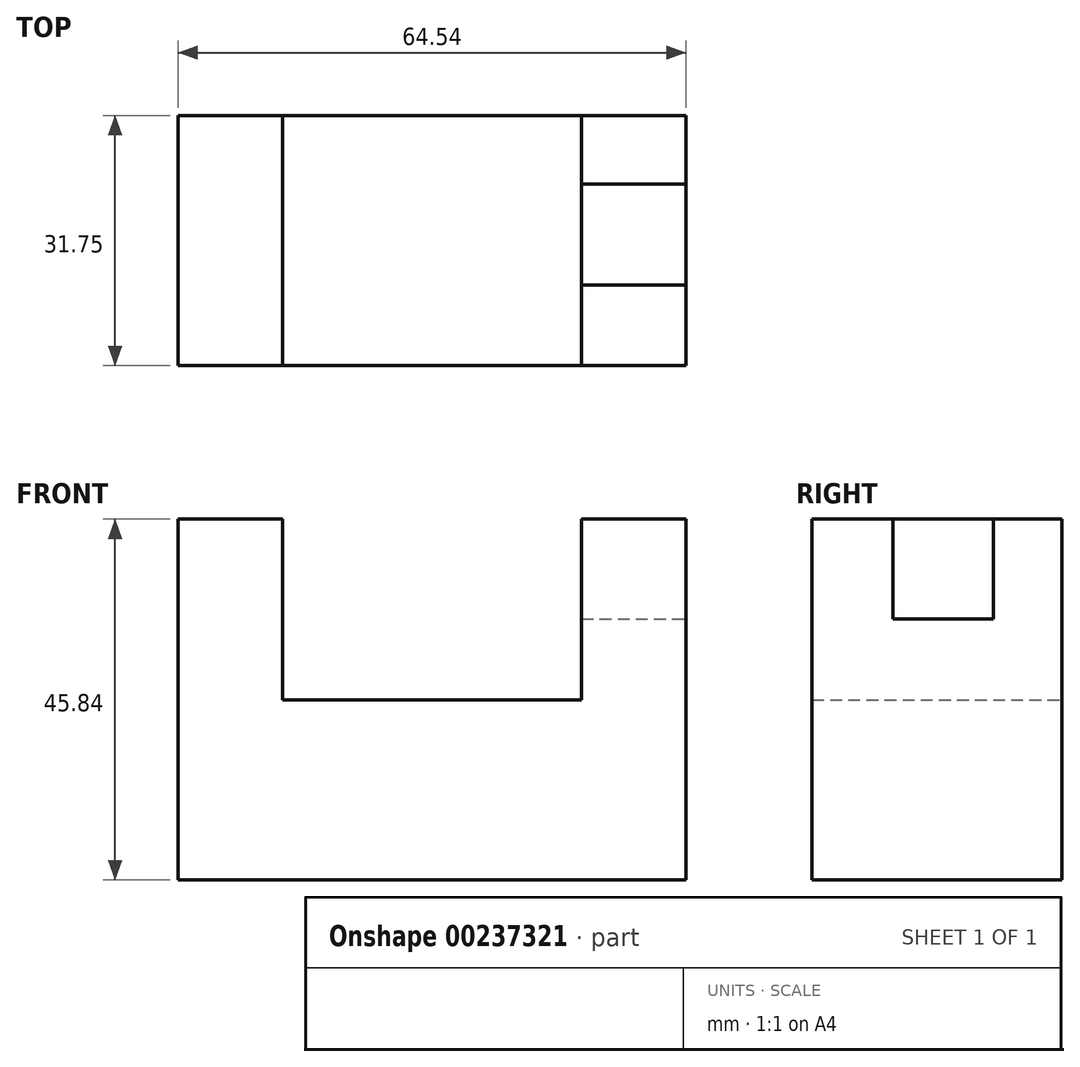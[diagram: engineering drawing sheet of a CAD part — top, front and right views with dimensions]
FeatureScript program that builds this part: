
annotation { "Feature Type Name" : "Feature", "Feature Type Description" : "" }
export const myFeature = defineFeature(function(context is Context, id is Id, definition is map)
    precondition{}
    {
        {
            var Q0;
            Q0=qCreatedBy(makeId("Front.planeOp"),FACE);
            var sketch = newSketch(context, id + "F0", { "sketchPlane" : qUnion([Q0])});
            skLineSegment(sketch, "E0.bottom", {"start": v(0, 0) * mm, "end": v(64.54, 0) * mm});
            skLineSegment(sketch, "E0.top", {"start": v(0, 45.84) * mm, "end": v(13.29, 45.84) * mm});
            skLineSegment(sketch, "E0.left", {"start": v(0, 0) * mm, "end": v(0, 45.84) * mm});
            skLineSegment(sketch, "E0.right", {"start": v(64.54, 0) * mm, "end": v(64.54, 45.84) * mm});
            skLineSegment(sketch, "E1.bottom", {"start": v(13.29, 22.87) * mm, "end": v(51.25, 22.87) * mm});
            skLineSegment(sketch, "E1.left", {"start": v(13.29, 22.87) * mm, "end": v(13.29, 45.84) * mm});
            skLineSegment(sketch, "E1.right", {"start": v(51.25, 22.87) * mm, "end": v(51.25, 45.84) * mm});
            skPoint(sketch, "E1.middle", {"position": v(32.27, 45.84) * mm});
            skPoint(sketch, "E1.top.start.orphan", {"position": v(13.29, 68.81) * mm});
            skPoint(sketch, "E2.orphan", {"position": v(51.25, 68.81) * mm});
            skLineSegment(sketch, "E3.trimOffspring", {"start": v(51.25, 45.84) * mm, "end": v(64.54, 45.84) * mm});
            skSolve(sketch);
        }
        {
            var Q0;
            Q0=makeQuery(id+"F0.imprint","IMPRINT",FACE,{"disambiguationData":[TD([[makeQuery(id+"F0.imprint","IMPRINT",EDGE,{"derivedFrom":sQuery(id+"F0.wireOp",EDGE,"E0.bottom")}),1.0]])]});
            extrude(context, id + "F1", {"entities" : qUnion([Q0]), "depth" : 31.75 * mm});
        }
        {
            var Q0;
            Q0=makeQuery(id+"F1.opExtrude","SWEPT_FACE",FACE,{"disambiguationData":[OSD([sQuery(id+"F0.wireOp",EDGE,"E3.trimOffspring")])]});
            var sketch = newSketch(context, id + "F2", { "sketchPlane" : qUnion([Q0])});
            skLineSegment(sketch, "E4", {"start": v(51.25, -21.52) * mm, "end": v(64.54, -21.52) * mm});
            skLineSegment(sketch, "E5", {"start": v(64.54, -21.52) * mm, "end": v(64.54, -8.73) * mm});
            skLineSegment(sketch, "E6", {"start": v(64.54, -8.73) * mm, "end": v(51.25, -8.73) * mm});
            skPoint(sketch, "E7", {"position": v(51.25, -15.88) * mm});
            skLineSegment(sketch, "E8", {"start": v(51.25, -8.73) * mm, "end": v(51.25, -21.52) * mm});
            skSolve(sketch);
        }
        {
            var Q0;
            Q0=makeQuery(id+"F2.imprint","IMPRINT",FACE,{"disambiguationData":[TD([[makeQuery(id+"F2.imprint","IMPRINT",EDGE,{"derivedFrom":sQuery(id+"F2.wireOp",EDGE,"E4")}),1.0]])]});
            extrude(context, id + "F3", {"entities" : qUnion([Q0]), "operationType" : NewBodyOperationType.REMOVE, "oppositeDirection" : true, "depth" : 12.7 * mm});
        }
    });
